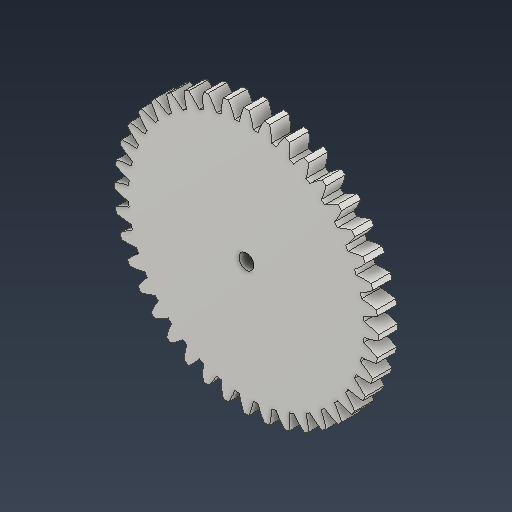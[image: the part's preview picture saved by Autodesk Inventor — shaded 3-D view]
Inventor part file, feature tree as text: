
AUTODESK INVENTOR PART (.ipt)
format: ipt  version: 2025.3 (Build 293356000, 356)  size: 325,632 bytes
history: native  units: mm (DEFAULTED — no unit token found)
features: plane x3, other x3, extrude x2, sketch x2
ambient origin geometry x8: Origin, YZ Plane, XZ Plane, XY Plane, X Axis, Y Axis, Z Axis, Center Point
bodies: Solid1 (feature_tree)
feature tree (10):
  extrude  "Extrusion1"  Depth=3.0mm TaperAngle=0.0deg
  plane  "Work Plane2"
  plane  "Work Plane8"
  plane  "Work Plane9"
  other  "正齒輪"
  extrude  "擠出2"  Depth=10.0mm
  sketch  "Sketch1"  dims[d0=41.249066mm d1=3.0mm d2=0.0mm d3=40.0mm d4=10.0mm d5=0.0mm d16=23.624533mm d17=0.0mm d34=0.785398mm d39=0.0mm d41=0.0mm d43=23.624533mm d46=23.624533mm d47=0.0mm d48=0.0mm d49=2.35mm d50=10.0mm d51=0.0mm]
  other  "Srf1"
  sketch  "草圖3"
  other  "節圓直徑"
